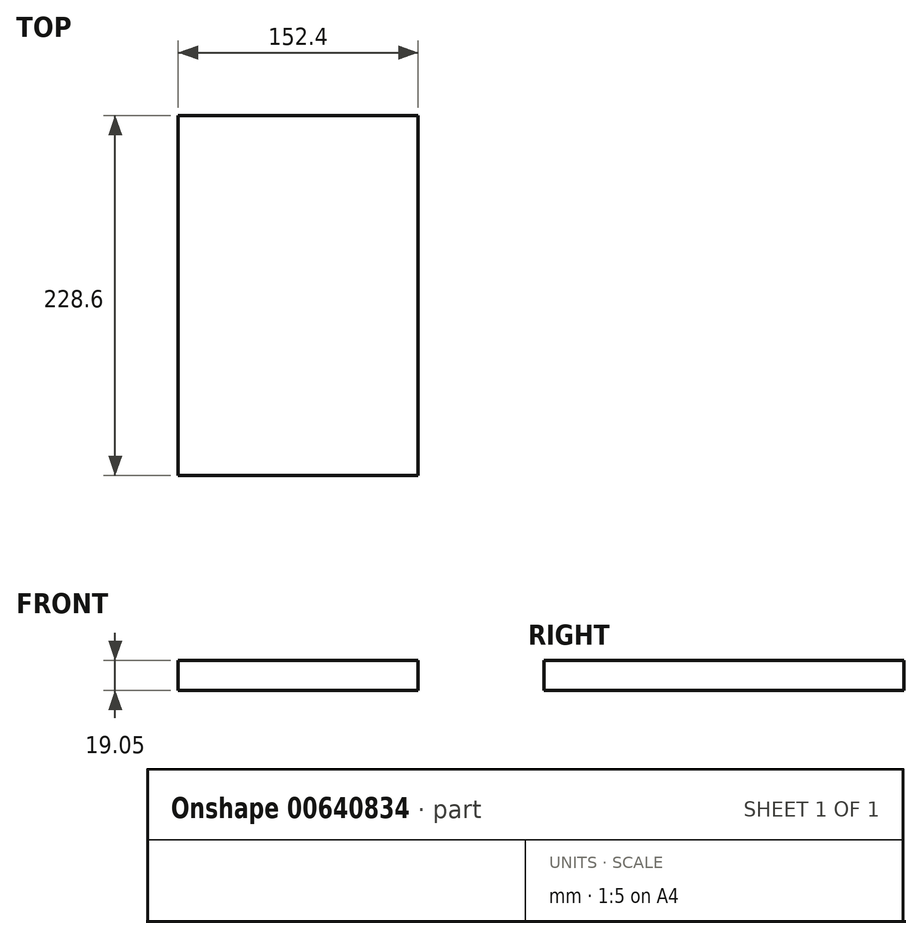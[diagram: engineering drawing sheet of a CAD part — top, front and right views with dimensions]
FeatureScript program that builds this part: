
annotation { "Feature Type Name" : "Feature", "Feature Type Description" : "" }
export const myFeature = defineFeature(function(context is Context, id is Id, definition is map)
    precondition{}
    {
        {
            var Q0;
            Q0=qCreatedBy(makeId("Top.planeOp"),FACE);
            var sketch = newSketch(context, id + "F0", { "sketchPlane" : qUnion([Q0])});
            skLineSegment(sketch, "E0.bottom", {"start": v(-76.2, 114.3) * mm, "end": v(76.2, 114.3) * mm});
            skLineSegment(sketch, "E0.top", {"start": v(-76.2, -114.3) * mm, "end": v(76.2, -114.3) * mm});
            skLineSegment(sketch, "E0.left", {"start": v(-76.2, 114.3) * mm, "end": v(-76.2, -114.3) * mm});
            skLineSegment(sketch, "E0.right", {"start": v(76.2, 114.3) * mm, "end": v(76.2, -114.3) * mm});
            skPoint(sketch, "E0.middle", {"position": v(0, 0) * mm});
            skSolve(sketch);
        }
        {
            var Q0;
            Q0=makeQuery(id+"F0.imprint","IMPRINT",FACE,{"disambiguationData":[TD([[makeQuery(id+"F0.imprint","IMPRINT",EDGE,{"derivedFrom":sQuery(id+"F0.wireOp",EDGE,"E0.bottom")}),-1.0]])]});
            extrude(context, id + "F1", {"entities" : qUnion([Q0]), "depth" : 19.05 * mm, "offsetDistance" : 25.4 * mm});
        }
    });
